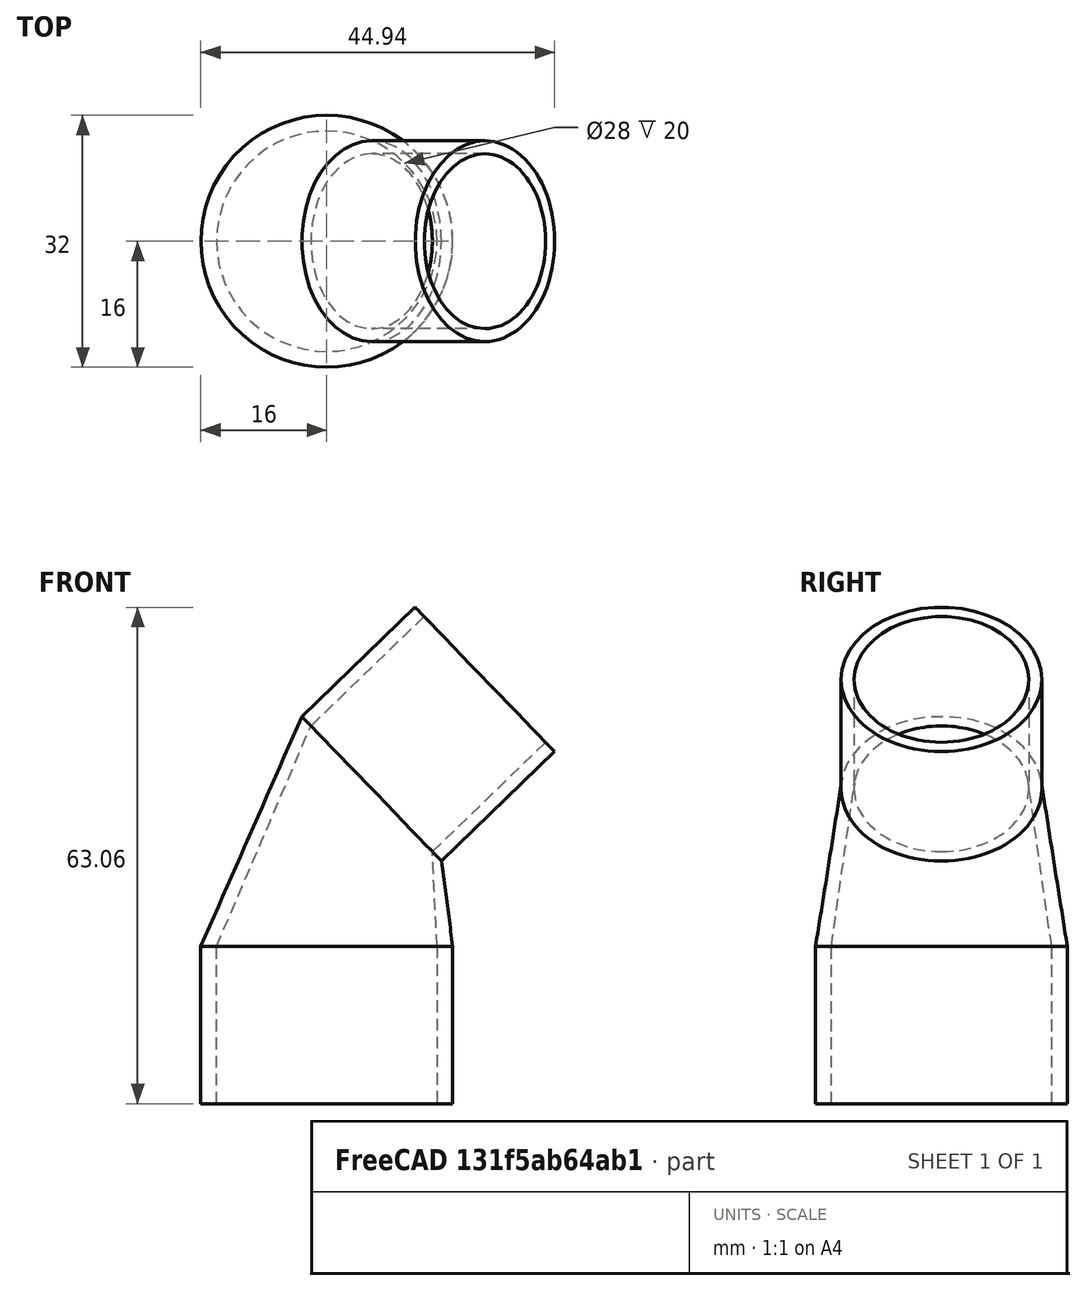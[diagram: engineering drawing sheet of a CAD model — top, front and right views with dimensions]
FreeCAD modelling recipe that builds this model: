
FCSTD DOCUMENT  (FreeCAD 0.19R20802 (Git))
Label: NIV_CPAP_Knuckle
License: All rights reserved
LicenseURL: http://en.wikipedia.org/wiki/All_rights_reserved
objects: TechDraw::DrawViewDimension×9, Sketcher::SketchObject×2, PartDesign::Pad×2, TechDraw::DrawProjGroupItem×2, PartDesign::Point×1, PartDesign::Plane×1, PartDesign::AdditiveLoft×1, PartDesign::Body×1, TechDraw::DrawSVGTemplate×1, TechDraw::DrawProjGroup×1, TechDraw::DrawViewAnnotation×1, TechDraw::DrawPage×1
note: 11 computed .brp shape members not serialized (recipe doc carries the construction recipe); baked Part::Feature solids carry a one-line shape summary decoded from their .brp

FEATURE [Sketcher::SketchObject] Sketch
  MapMode = 5
  Support = -> [XY_Plane]
  sketch-geometry (2):
    g0: Circle CenterX=0 CenterY=0 CenterZ=0 NormalX=0 NormalY=0 NormalZ=1 AngleXU=0 Radius=16
    g1: Circle CenterX=0 CenterY=0 CenterZ=0 NormalX=0 NormalY=0 NormalZ=1 AngleXU=0 Radius=14
  constraints (4):
    c: Coincident(g0,g-1)
    c: Radius(g0) = 16
    c: Coincident(g1,g0)
    c: Radius(g1) = 14
FEATURE [PartDesign::Point] DatumPoint
  AttacherType = Attacher::AttachEnginePoint
  AttachmentOffset = pos=(5.69542,0,20) rot=(0,0,1;0rad)
  MapMode = 32
  Placement = pos=(5.69542,0,20) rot=(0,0,1;0rad)
  Support = -> [XY_Plane]
FEATURE [PartDesign::Plane] DatumPlane
  AttachmentOffset = pos=(0,0,0) rot=(0,1,0;0.802851rad)
  Length = 99.5786
  MapMode = 2
  Placement = pos=(5.69542,0,20) rot=(0,1,0;0.802851rad)
  ResizeMode = 0
  Support = -> [DatumPoint]
  Width = 63.1477
FEATURE [Sketcher::SketchObject] Sketch001
  MapMode = 5
  Placement = pos=(5.69542,0,20) rot=(0,1,0;0.802851rad)
  Support = -> [DatumPlane]
  sketch-geometry (2):
    g0: Circle CenterX=0 CenterY=0 CenterZ=0 NormalX=0 NormalY=0 NormalZ=1 AngleXU=0 Radius=12.75
    g1: Circle CenterX=0 CenterY=0 CenterZ=0 NormalX=0 NormalY=0 NormalZ=1 AngleXU=0 Radius=11.1
  constraints (6):
    c: PointOnObject(g0,g-2)
    c: Radius(g0) = 12.75
    c: PointOnObject(g1,g-2)
    c: Radius(g1) = 11.1
    c: PointOnObject(g1,g-1)
    c: PointOnObject(g0,g-1)
FEATURE [PartDesign::AdditiveLoft] AdditiveLoft
  Closed = true
  Profile = -> Sketch
  Ruled = false
  Sections = -> [Sketch001]
FEATURE [PartDesign::Pad] Pad
  BaseFeature = -> AdditiveLoft
  Length = 20
  Length2 = 100
  Profile = -> AdditiveLoft [Face3]
  Type = 0
FEATURE [PartDesign::Pad] Pad001
  BaseFeature = -> Pad
  Length = 20
  Length2 = 100
  Profile = -> Pad [Face1]
  Type = 0
FEATURE [PartDesign::Body] Body
  Group = -> [Sketch,DatumPoint,DatumPlane,Sketch001,AdditiveLoft,Pad,Pad001]
  Origin = -> Origin
  Tip = -> Pad001
FEATURE [TechDraw::DrawSVGTemplate] Template
  Height = 297
  Orientation = 0
  Width = 210
FEATURE [TechDraw::DrawProjGroupItem] ProjItem  label="Front"
  CoarseView = false
  Direction = (0,-1,0)
  Focus = 100
  HardHidden = true
  IsoCount = 0
  IsoHidden = false
  IsoVisible = false
  LockPosition = true
  Perspective = false
  Rotation = 0
  RotationVector = (1,0,0)
  Scale = 2
  ScaleType = 2
  SeamHidden = false
  SeamVisible = true
  SmoothHidden = false
  SmoothVisible = true
  Source = -> [Pad001]
  Type = 0
  X = 0
  XDirection = (1,0,0)
  Y = 0
FEATURE [TechDraw::DrawProjGroupItem] ProjItem001  label="FrontTopRight"
  CoarseView = false
  Direction = (0.57735,-0.57735,0.57735)
  Focus = 100
  HardHidden = false
  IsoCount = 0
  IsoHidden = false
  IsoVisible = false
  LockPosition = false
  Perspective = false
  Rotation = 0
  RotationVector = (1,0,0)
  ScaleType = 2
  SeamHidden = false
  SeamVisible = false
  SmoothHidden = false
  SmoothVisible = true
  Source = -> [Pad001]
  Type = 7
  X = 74.9056
  XDirection = (0.707107,0.707107,0)
  Y = 136.952
FEATURE [TechDraw::DrawProjGroup] ProjGroup
  Anchor = -> ProjItem
  AutoDistribute = false
  LockPosition = false
  ProjectionType = 0
  Rotation = 0
  Scale = 2
  ScaleType = 0
  Source = -> [Pad001]
  Views = -> [ProjItem,ProjItem001]
  X = 73.8824
  Y = 94.2176
  spacingX = 15
  spacingY = 15
FEATURE [TechDraw::DrawViewDimension] Dimension
  Arbitrary = false
  FormatSpec = %.2f
  Inverted = false
  LockPosition = false
  MeasureType = 1
  OverTolerance = 0
  References2D = -> [ProjItem]
  Rotation = 0
  Scale = 2
  ScaleType = 0
  TheoreticalExact = false
  Type = 2
  UnderTolerance = 0
  X = -63.0321
  Y = -25.3845
FEATURE [TechDraw::DrawViewDimension] Dimension001
  Arbitrary = false
  FormatSpec = %.2f
  Inverted = false
  LockPosition = false
  MeasureType = 1
  OverTolerance = 0
  References2D = -> [ProjItem]
  Rotation = 0
  Scale = 2
  ScaleType = 0
  TheoreticalExact = false
  Type = 1
  UnderTolerance = 0
  X = -49.1185
  Y = 28.352
FEATURE [TechDraw::DrawViewDimension] Dimension002
  Arbitrary = false
  FormatSpec = Ø%.2f
  Inverted = false
  LockPosition = false
  MeasureType = 1
  OverTolerance = 0
  References2D = -> [ProjItem]
  Rotation = 0
  Scale = 2
  ScaleType = 0
  TheoreticalExact = false
  Type = 0
  UnderTolerance = 0
  X = 52.3995
  Y = 64.3113
FEATURE [TechDraw::DrawViewDimension] Dimension003
  Arbitrary = false
  FormatSpec = Ø%.2f
  Inverted = false
  LockPosition = false
  MeasureType = 1
  OverTolerance = 0
  References2D = -> [ProjItem]
  Rotation = 0
  Scale = 2
  ScaleType = 0
  TheoreticalExact = false
  Type = 0
  UnderTolerance = 0
  X = 43.3876
  Y = 55.2598
FEATURE [TechDraw::DrawViewDimension] Dimension004
  Arbitrary = false
  FormatSpec = Ø%.2f
  Inverted = false
  LockPosition = false
  MeasureType = 1
  OverTolerance = 0
  References2D = -> [ProjItem]
  Rotation = 0
  Scale = 2
  ScaleType = 0
  TheoreticalExact = false
  Type = 1
  UnderTolerance = 0
  X = -4.60843
  Y = -82.3904
FEATURE [TechDraw::DrawViewDimension] Dimension005
  Arbitrary = false
  FormatSpec = Ø%.2f
  Inverted = false
  LockPosition = false
  MeasureType = 1
  OverTolerance = 0
  References2D = -> [ProjItem]
  Rotation = 0
  Scale = 2
  ScaleType = 0
  TheoreticalExact = false
  Type = 1
  UnderTolerance = 0
  X = -6.72563
  Y = -71.6203
FEATURE [TechDraw::DrawViewDimension] Dimension006
  Arbitrary = false
  FormatSpec = %.2f
  Inverted = false
  LockPosition = false
  MeasureType = 1
  OverTolerance = 0
  References2D = -> [ProjItem]
  Rotation = 0
  Scale = 2
  ScaleType = 0
  TheoreticalExact = false
  Type = 6
  UnderTolerance = 0
  X = 66.838
  Y = -28.6449
FEATURE [TechDraw::DrawViewDimension] Dimension007
  Arbitrary = false
  FormatSpec = %.2f
  Inverted = false
  LockPosition = false
  MeasureType = 1
  OverTolerance = 0
  References2D = -> [ProjItem]
  Rotation = 0
  Scale = 2
  ScaleType = 0
  TheoreticalExact = false
  Type = 0
  UnderTolerance = 0
  X = -11.2445
  Y = 62.7955
FEATURE [TechDraw::DrawViewDimension] Dimension008
  Arbitrary = false
  FormatSpec = %.2f
  Inverted = false
  LockPosition = false
  MeasureType = 1
  OverTolerance = 0
  References2D = -> [ProjItem]
  Rotation = 0
  Scale = 2
  ScaleType = 0
  TheoreticalExact = false
  Type = 2
  UnderTolerance = 0
  X = -50.5785
  Y = -42.3349
FEATURE [TechDraw::DrawViewAnnotation] Annotation
  Caption = Scale 2:1
  Font = osifont
  LineSpace = 80
  LockPosition = false
  MaxWidth = -1
  Rotation = 0
  Scale = 2
  ScaleType = 0
  Text = NIV_CPAP_Knuckle
  TextSize = 5
  TextStyle = 0
  X = 28.9316
  Y = 283.968
FEATURE [TechDraw::DrawPage] Page
  KeepUpdated = true
  NextBalloonIndex = 1
  ProjectionType = 0
  Scale = 2
  Template = -> Template
  Views = -> [ProjGroup,Dimension,Dimension001,Dimension002,Dimension003,Dimension004,Dimension005,Dimension006,Dimension007,Dimension008,Annotation]
